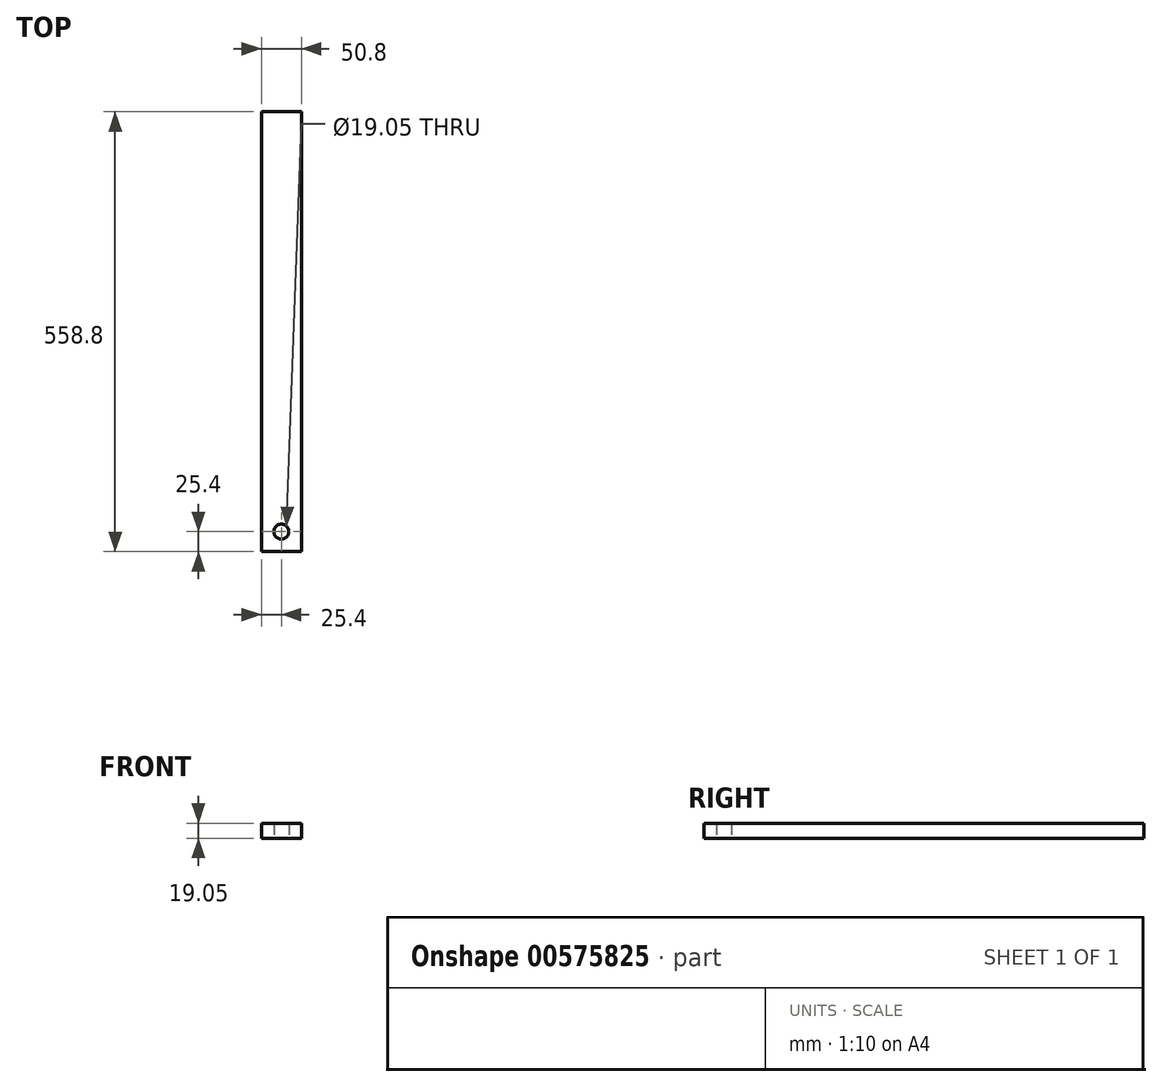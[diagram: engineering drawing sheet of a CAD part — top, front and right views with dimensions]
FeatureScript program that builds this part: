
annotation { "Feature Type Name" : "Feature", "Feature Type Description" : "" }
export const myFeature = defineFeature(function(context is Context, id is Id, definition is map)
    precondition{}
    {
        {
            var Q0;
            Q0=qCreatedBy(makeId("Top.planeOp"),FACE);
            var sketch = newSketch(context, id + "F0", { "sketchPlane" : qUnion([Q0])});
            skLineSegment(sketch, "E0.bottom", {"start": v(0, 0) * mm, "end": v(50.8, 0) * mm});
            skLineSegment(sketch, "E0.top", {"start": v(0, 508) * mm, "end": v(50.8, 508) * mm});
            skLineSegment(sketch, "E0.left", {"start": v(0, 0) * mm, "end": v(0, 508) * mm});
            skLineSegment(sketch, "E0.right", {"start": v(50.8, 0) * mm, "end": v(50.8, 508) * mm});
            skLineSegment(sketch, "E1.top", {"start": v(0, -50.8) * mm, "end": v(50.8, -50.8) * mm});
            skLineSegment(sketch, "E1.left", {"start": v(0, 0) * mm, "end": v(0, -50.8) * mm});
            skLineSegment(sketch, "E1.right", {"start": v(50.8, 0) * mm, "end": v(50.8, -50.8) * mm});
            skCircle(sketch, "E2", {"center": v(25.4, -25.4) * mm, "radius": 9.53 * mm});
            skPoint(sketch, "E2.centerSnap0", {"position": v(25.4, 0) * mm});
            skPoint(sketch, "E2.centerSnap1", {"position": v(0, -25.4) * mm});
            skSolve(sketch);
        }
        {
            var Q0;
            Q0 = qSketchRegion(id + "F0", true);
            extrude(context, id + "F1", {"entities" : qUnion([Q0]), "depth" : 19.05 * mm, "offsetDistance" : 25.4 * mm});
        }
    });
